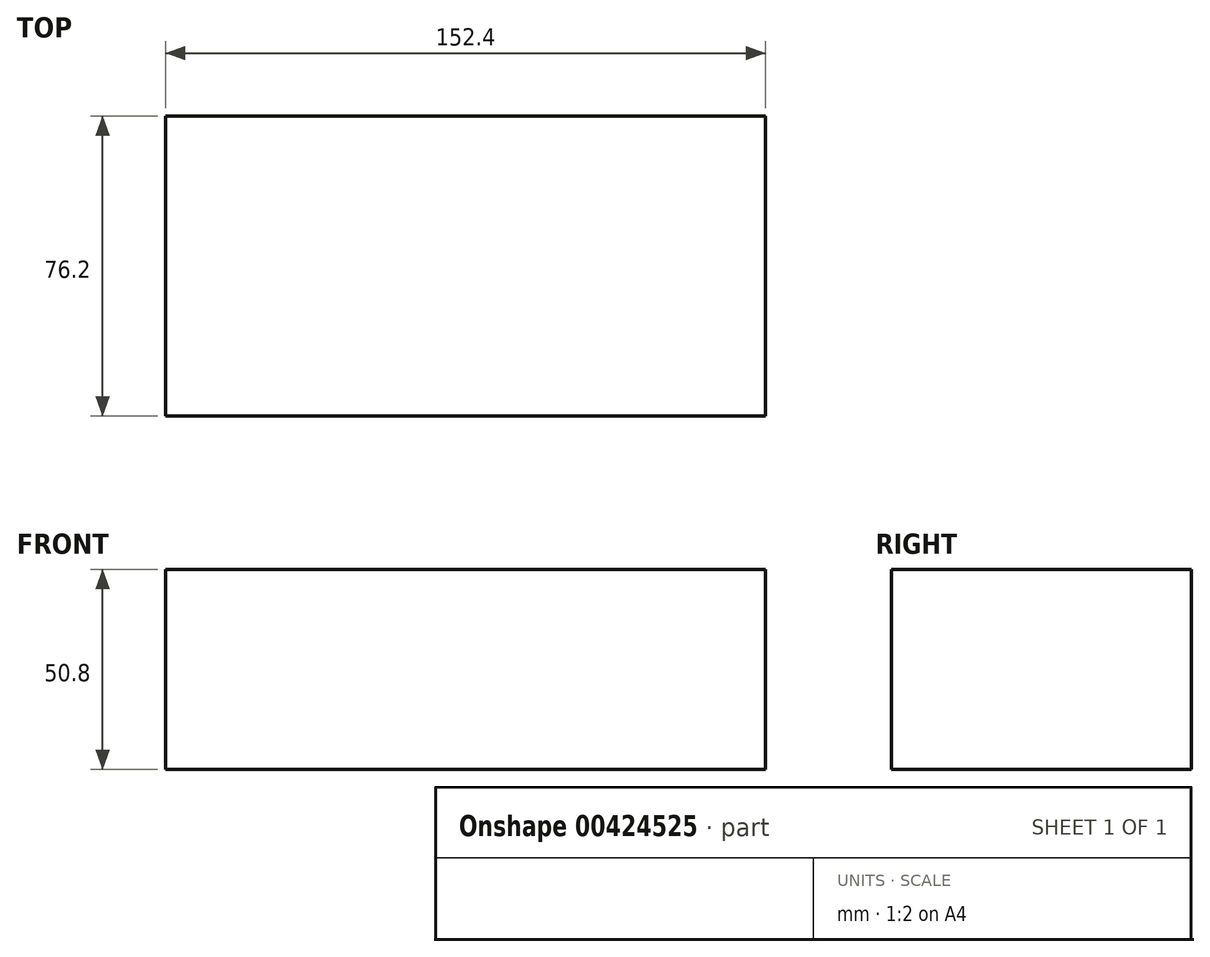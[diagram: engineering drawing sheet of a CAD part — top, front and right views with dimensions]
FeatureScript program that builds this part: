
annotation { "Feature Type Name" : "Feature", "Feature Type Description" : "" }
export const myFeature = defineFeature(function(context is Context, id is Id, definition is map)
    precondition{}
    {
        {
            var Q0;
            Q0=qCreatedBy(makeId("Front.planeOp"),FACE);
            var sketch = newSketch(context, id + "F0", { "sketchPlane" : qUnion([Q0])});
            skLineSegment(sketch, "E0", {"start": v(0, 0) * mm, "end": v(152.4, 0) * mm});
            skLineSegment(sketch, "E1", {"start": v(0, 0) * mm, "end": v(0, 50.8) * mm});
            skLineSegment(sketch, "E2", {"start": v(0, 50.8) * mm, "end": v(152.4, 50.8) * mm});
            skLineSegment(sketch, "E3", {"start": v(152.4, 0) * mm, "end": v(152.4, 50.8) * mm});
            skSolve(sketch);
        }
        {
            var Q0;
            Q0=makeQuery(id+"F0.imprint","IMPRINT",FACE,{"disambiguationData":[TD([[makeQuery(id+"F0.imprint","IMPRINT",EDGE,{"derivedFrom":sQuery(id+"F0.wireOp",EDGE,"E0")}),1.0]])]});
            extrude(context, id + "F1", {"entities" : qUnion([Q0]), "oppositeDirection" : true, "depth" : 76.2 * mm});
        }
    });
